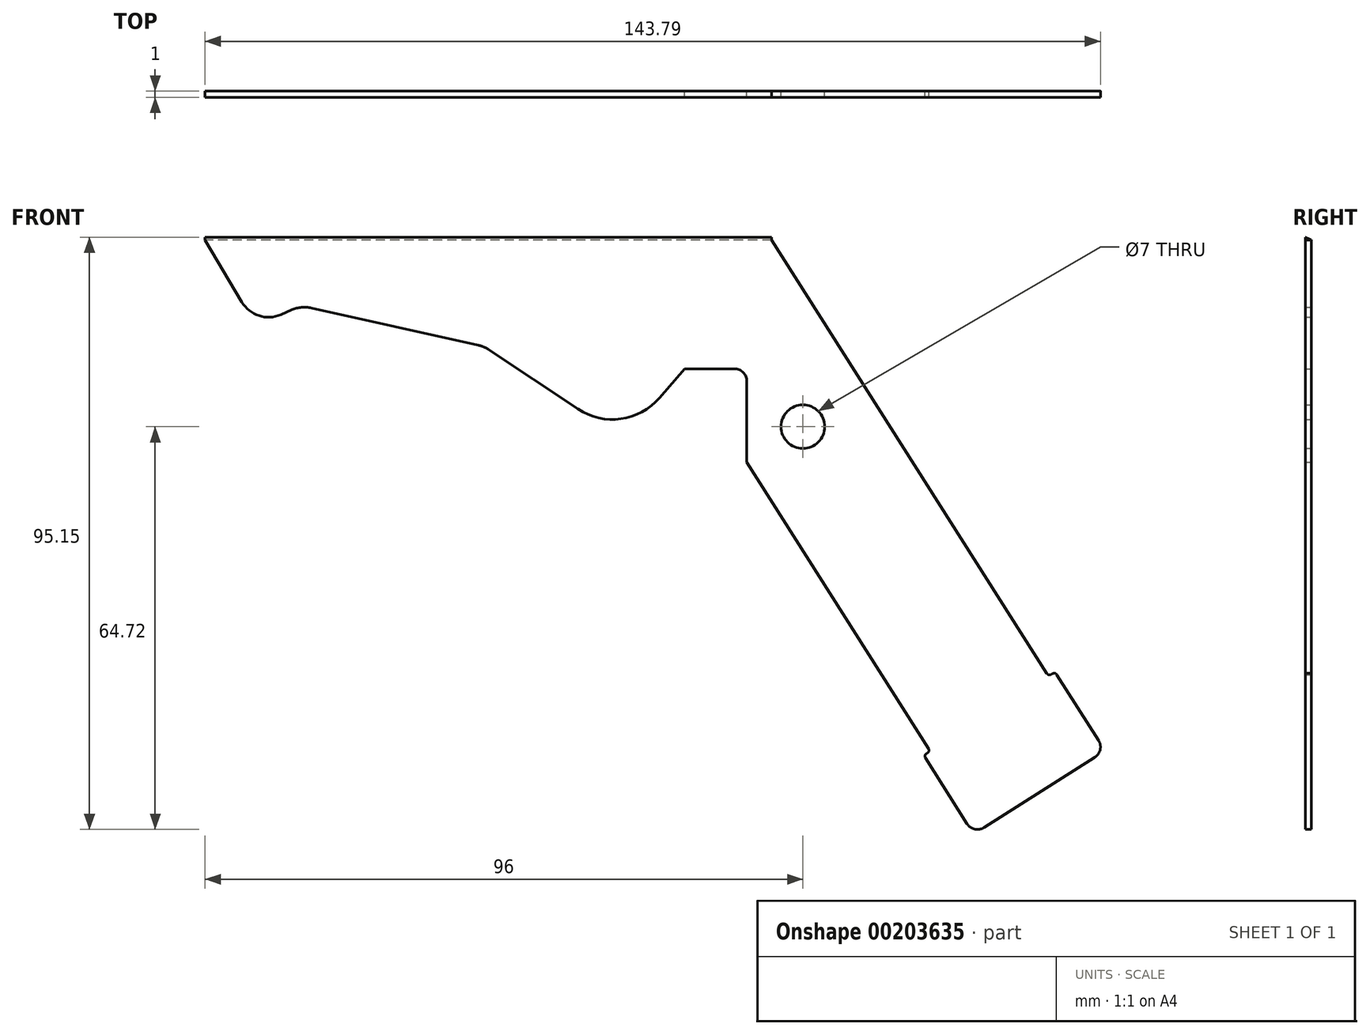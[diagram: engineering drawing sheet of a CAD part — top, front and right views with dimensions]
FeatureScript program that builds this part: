
annotation { "Feature Type Name" : "Feature", "Feature Type Description" : "" }
export const myFeature = defineFeature(function(context is Context, id is Id, definition is map)
    precondition{}
    {
        {
            var Q0;
            Q0=qCreatedBy(makeId("Front.planeOp"),FACE);
            var sketch = newSketch(context, id + "F0", { "sketchPlane" : qUnion([Q0])});
            skLineSegment(sketch, "E0", {"start": v(0, 0) * mm, "end": v(-91, 0) * mm});
            skLineSegment(sketch, "E1", {"start": v(-91, 0) * mm, "end": v(-85.11, -9.96) * mm});
            skLineSegment(sketch, "E2", {"start": v(-78.8, -12) * mm, "end": v(-77.03, -11.22) * mm});
            skLineSegment(sketch, "E3", {"start": v(-73.93, -10.92) * mm, "end": v(-47.16, -16.89) * mm});
            skLineSegment(sketch, "E4", {"start": v(-45.47, -17.6) * mm, "end": v(-31.14, -27.16) * mm});
            skLineSegment(sketch, "E5", {"start": v(-18.01, -25.36) * mm, "end": v(-14, -20.7) * mm});
            skLineSegment(sketch, "E6", {"start": v(-14, -20.7) * mm, "end": v(-6, -20.7) * mm});
            skLineSegment(sketch, "E7", {"start": v(-4, -22.7) * mm, "end": v(-4, -35.7) * mm});
            skLineSegment(sketch, "E8", {"start": v(-4, -35.7) * mm, "end": v(25.2, -81.72) * mm});
            skLineSegment(sketch, "E9", {"start": v(33.5, -94.8) * mm, "end": v(52.5, -82.75) * mm});
            skLineSegment(sketch, "E10", {"start": v(44.2, -69.66) * mm, "end": v(0, 0) * mm});
            skCircle(sketch, "E11", {"center": v(5, -30) * mm, "radius": 3.5 * mm});
            skPoint(sketch, "E12.visualSharp", {"position": v(-82.86, -13.77) * mm});
            skArc(sketch, "E12.filletArc", {"start": v(-85.11, -9.96) * mm, "mid": v(-82.34, -12.18) * mm, "end": v(-78.8, -12) * mm});
            skPoint(sketch, "E13.visualSharp", {"position": v(-75.53, -10.57) * mm});
            skArc(sketch, "E13.filletArc", {"start": v(-73.93, -10.92) * mm, "mid": v(-75.5, -10.83) * mm, "end": v(-77.03, -11.22) * mm});
            skPoint(sketch, "E14.visualSharp", {"position": v(-46.25, -17.1) * mm});
            skArc(sketch, "E14.filletArc", {"start": v(-45.47, -17.6) * mm, "mid": v(-46.28, -17.17) * mm, "end": v(-47.16, -16.89) * mm});
            skPoint(sketch, "E15.visualSharp", {"position": v(-23.78, -32.07) * mm});
            skArc(sketch, "E15.filletArc", {"start": v(-31.14, -27.16) * mm, "mid": v(-24.24, -28.75) * mm, "end": v(-18.01, -25.36) * mm});
            skPoint(sketch, "E16.visualSharp", {"position": v(-4, -20.7) * mm});
            skArc(sketch, "E16.filletArc", {"start": v(-4, -22.7) * mm, "mid": v(-4.59, -21.28) * mm, "end": v(-6, -20.7) * mm});
            skLineSegment(sketch, "E17", {"start": v(51.86, -83.15) * mm, "end": v(52.5, -82.75) * mm});
            skLineSegment(sketch, "E18", {"start": v(52.48, -80.4) * mm, "end": v(45.79, -69.84) * mm});
            skLineSegment(sketch, "E19", {"start": v(25.04, -82.4) * mm, "end": v(24.83, -82.54) * mm});
            skLineSegment(sketch, "E20", {"start": v(24.68, -83.23) * mm, "end": v(31.37, -93.79) * mm});
            skLineSegment(sketch, "E21", {"start": v(33.5, -94.8) * mm, "end": v(34.13, -94.4) * mm});
            skPoint(sketch, "E22.visualSharp", {"position": v(45.52, -69.42) * mm});
            skArc(sketch, "E22.filletArc", {"start": v(45.79, -69.84) * mm, "mid": v(45.47, -69.62) * mm, "end": v(45.1, -69.68) * mm});
            skPoint(sketch, "E23.visualSharp", {"position": v(53.55, -82.08) * mm});
            skPoint(sketch, "E24.visualSharp", {"position": v(32.44, -95.48) * mm});
            skArc(sketch, "E24.filletArc", {"start": v(31.37, -93.79) * mm, "mid": v(32.62, -94.67) * mm, "end": v(34.13, -94.4) * mm});
            skPoint(sketch, "E25.visualSharp", {"position": v(24.4, -82.8) * mm});
            skArc(sketch, "E26.filletArc", {"start": v(25.04, -82.4) * mm, "mid": v(25.26, -82.1) * mm, "end": v(25.2, -81.72) * mm});
            skLineSegment(sketch, "E27", {"start": v(45.1, -69.68) * mm, "end": v(44.88, -69.82) * mm});
            skPoint(sketch, "E28.visualSharp", {"position": v(44.46, -70.09) * mm});
            skArc(sketch, "E28.filletArc", {"start": v(44.2, -69.66) * mm, "mid": v(44.5, -69.88) * mm, "end": v(44.88, -69.82) * mm});
            skArc(sketch, "E29.filletArc", {"start": v(24.83, -82.54) * mm, "mid": v(24.6, -82.85) * mm, "end": v(24.68, -83.23) * mm});
            skArc(sketch, "E30.filletArc", {"start": v(51.86, -83.15) * mm, "mid": v(52.74, -81.9) * mm, "end": v(52.48, -80.4) * mm});
            skSolve(sketch);
        }
        {
            var Q0;
            Q0 = qSketchRegion(id + "F0", true);
            extrude(context, id + "F1", {"entities" : qUnion([Q0]), "depth" : 1 * mm});
        }
        {
            var Q0;
            Q0=qCreatedBy(makeId("Right.planeOp"),FACE);
            var sketch = newSketch(context, id + "F2", { "sketchPlane" : qUnion([Q0])});
            skCircle(sketch, "E31", {"center": v(7, 17.72) * mm, "radius": 19.05 * mm});
            skLineSegment(sketch, "E32", {"start": v(-1, 0) * mm, "end": v(-1, 0.43) * mm});
            skLineSegment(sketch, "E33.0", {"start": v(-1, 0) * mm, "end": v(0, 0) * mm});
            skSolve(sketch);
        }
        {
            var Q0;
            {var subQ0=sQuery(id+"F2.wireOp",EDGE,"E32");Q0=makeQuery(id+"F2.imprint","IMPRINT",FACE,{"disambiguationData":[TD([[makeQuery(id+"F2.imprint","IMPRINT",EDGE,{"derivedFrom":subQ0}),-1.0]])]});}
            var Q1;
            Q1=makeQuery(id+"F1.opExtrude","CAP_VERTEX",VERTEX,{"disambiguationData":[OSD([sQuery(id+"F0.wireOp",EDGE,"E0"),sQuery(id+"F0.wireOp",EDGE,"E1")])],"isStart":false});
            extrude(context, id + "F3", {"entities" : qUnion([Q0]), "operationType" : NewBodyOperationType.ADD, "endBound" : BoundingType.UP_TO_VERTEX, "oppositeDirection" : true, "endBoundEntityVertex" : qUnion([Q1]), "depth" : 25 * mm});
        }
    });
